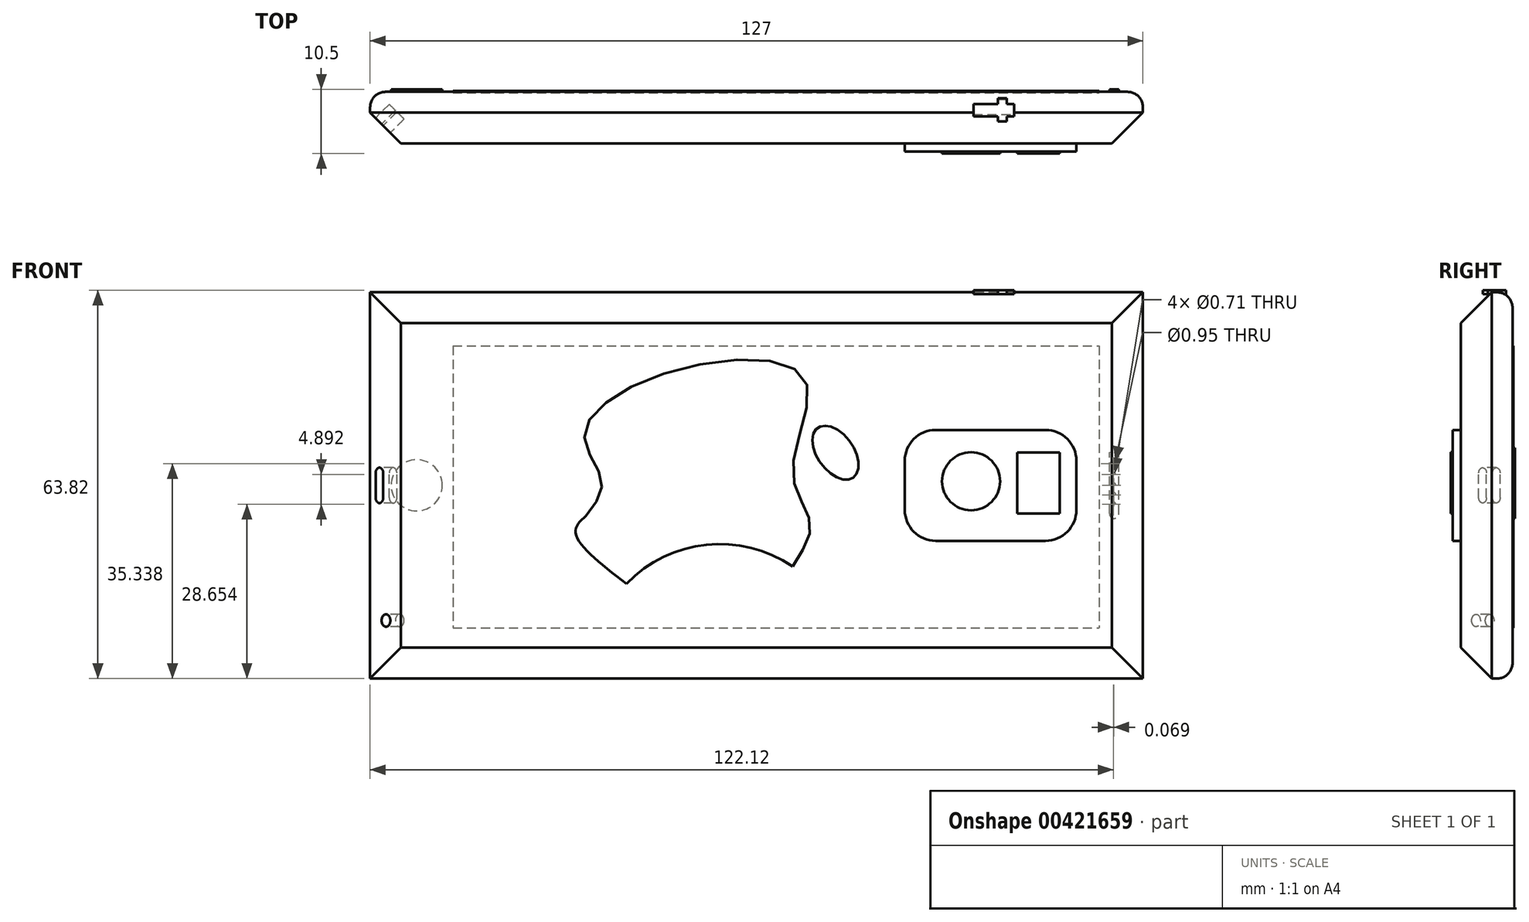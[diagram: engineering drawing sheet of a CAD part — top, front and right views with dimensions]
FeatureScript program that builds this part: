
annotation { "Feature Type Name" : "Feature", "Feature Type Description" : "" }
export const myFeature = defineFeature(function(context is Context, id is Id, definition is map)
    precondition{}
    {
        {
            var Q0;
            Q0=qCreatedBy(makeId("Front.planeOp"),FACE);
            var sketch = newSketch(context, id + "F0", { "sketchPlane" : qUnion([Q0])});
            skLineSegment(sketch, "E0.bottom", {"start": v(-64.83, 26.37) * mm, "end": v(62.17, 26.37) * mm});
            skLineSegment(sketch, "E0.top", {"start": v(-64.83, -37.13) * mm, "end": v(62.17, -37.13) * mm});
            skLineSegment(sketch, "E0.left", {"start": v(-64.83, 26.37) * mm, "end": v(-64.83, -37.13) * mm});
            skLineSegment(sketch, "E0.right", {"start": v(62.17, 26.37) * mm, "end": v(62.17, -37.13) * mm});
            skSolve(sketch);
        }
        {
            var Q0;
            Q0 = qSketchRegion(id + "F0", true);
            extrude(context, id + "F1", {"entities" : qUnion([Q0]), "depth" : 8.47 * mm});
        }
        {
            var Q0;
            Q0=makeQuery(id+"F1.opExtrude","CAP_FACE",FACE,{"disambiguationData":[OSD([sQuery(id+"F0.wireOp",EDGE,"E0.bottom"),sQuery(id+"F0.wireOp",EDGE,"E0.top"),sQuery(id+"F0.wireOp",EDGE,"E0.left"),sQuery(id+"F0.wireOp",EDGE,"E0.right")])],"isStart":true});
            fillet(context, id + "F2", {"entities" : qUnion([Q0]), "radius" : 2.54 * mm, "tangentPropagation" : true, "allowEdgeOverflow" : false});
        }
        {
            var Q0;
            Q0=makeQuery(id+"F1.opExtrude","CAP_FACE",FACE,{"disambiguationData":[OSD([sQuery(id+"F0.wireOp",EDGE,"E0.bottom"),sQuery(id+"F0.wireOp",EDGE,"E0.top"),sQuery(id+"F0.wireOp",EDGE,"E0.left"),sQuery(id+"F0.wireOp",EDGE,"E0.right")])],"isStart":true});
            var sketch = newSketch(context, id + "F3", { "sketchPlane" : qUnion([Q0])});
            skLineSegment(sketch, "E1.bottom", {"start": v(51.23, 17.56) * mm, "end": v(-54.97, 17.56) * mm});
            skLineSegment(sketch, "E1.top", {"start": v(51.23, -28.78) * mm, "end": v(-54.97, -28.78) * mm});
            skLineSegment(sketch, "E1.left", {"start": v(51.23, 17.56) * mm, "end": v(51.23, -28.78) * mm});
            skLineSegment(sketch, "E1.right", {"start": v(-54.97, 17.56) * mm, "end": v(-54.97, -28.78) * mm});
            skSolve(sketch);
        }
        {
            var Q0;
            Q0 = qSketchRegion(id + "F3", true);
            extrude(context, id + "F4", {"entities" : qUnion([Q0]), "endBound" : BoundingType.SYMMETRIC, "oppositeDirection" : true, "depth" : 0.28 * mm});
        }
        {
            var Q0;
            {var subQ0=sQuery(id+"F0.wireOp",EDGE,"E0.left");Q0=makeQuery(id+"F2.opFillet","BLEND_EDGE",EDGE,{"blendedFrom":[makeQuery(id+"F1.opExtrude","CAP_EDGE",EDGE,{"disambiguationData":[OSD([subQ0])],"isStart":true}),makeQuery(id+"F1.opExtrude","SWEPT_FACE",FACE,{"disambiguationData":[OSD([subQ0])]})],"blendedInto":[makeQuery(id+"F1.opExtrude","SWEPT_FACE",FACE,{"disambiguationData":[OSD([subQ0])]})]});}
            var Q1;
            Q1=makeQuery(id+"F1.opExtrude","CAP_EDGE",EDGE,{"disambiguationData":[OSD([sQuery(id+"F0.wireOp",EDGE,"E0.left")])],"isStart":false});
            var Q2;
            Q2=makeQuery(id+"F1.opExtrude","CAP_FACE",FACE,{"disambiguationData":[OSD([sQuery(id+"F0.wireOp",EDGE,"E0.bottom"),sQuery(id+"F0.wireOp",EDGE,"E0.top"),sQuery(id+"F0.wireOp",EDGE,"E0.left"),sQuery(id+"F0.wireOp",EDGE,"E0.right")])],"isStart":false});
            chamfer(context, id + "F5", {"entities" : qUnion([Q0, Q1, Q2]), "width" : 5.08 * mm, "tangentPropagation" : true});
        }
        {
            var Q0;
            Q0=makeQuery(id+"F1.opExtrude","CAP_FACE",FACE,{"disambiguationData":[OSD([sQuery(id+"F0.wireOp",EDGE,"E0.bottom"),sQuery(id+"F0.wireOp",EDGE,"E0.top"),sQuery(id+"F0.wireOp",EDGE,"E0.left"),sQuery(id+"F0.wireOp",EDGE,"E0.right")])],"isStart":true});
            var sketch = newSketch(context, id + "F6", { "sketchPlane" : qUnion([Q0])});
            skCircle(sketch, "E2", {"center": v(57.19, -5.38) * mm, "radius": 4.2 * mm});
            skPoint(sketch, "E2.centerSnap0", {"position": v(62.3, -5.38) * mm});
            skSolve(sketch);
        }
        {
            var Q0;
            Q0 = qSketchRegion(id + "F6", true);
            extrude(context, id + "F7", {"entities" : qUnion([Q0]), "depth" : 0.38 * mm});
        }
        {
            var Q0;
            Q0=makeQuery(id+"F1.opExtrude","CAP_FACE",FACE,{"disambiguationData":[OSD([sQuery(id+"F0.wireOp",EDGE,"E0.bottom"),sQuery(id+"F0.wireOp",EDGE,"E0.top"),sQuery(id+"F0.wireOp",EDGE,"E0.left"),sQuery(id+"F0.wireOp",EDGE,"E0.right")])],"isStart":true});
            var sketch = newSketch(context, id + "F8", { "sketchPlane" : qUnion([Q0])});
            skPoint(sketch, "E3.0.internal.snap0", {"position": v(-59.63, -5.38) * mm});
            skFitSpline(sketch, "E3", {"points": [v(-58.2, -5.38) * mm, v(-58.2, 0) * mm], "startDerivative": vector(0, 5.38) * mm, "endDerivative": vector(0, 5.38) * mm});
            skFitSpline(sketch, "E4", {"points": [v(-58.2, -5.38) * mm, v(-58.2, -10.03) * mm], "startDerivative": vector(0, -4.65) * mm, "endDerivative": vector(0, -4.65) * mm});
            skArc(sketch, "E5", {"start": v(-58.2, -10.03) * mm, "mid": v(-57.44, -10.81) * mm, "end": v(-56.67, -10.03) * mm});
            skLineSegment(sketch, "E6", {"start": v(-56.67, -10.03) * mm, "end": v(-56.67, 0) * mm});
            skArc(sketch, "E7", {"start": v(-56.67, 0) * mm, "mid": v(-57.44, 0.77) * mm, "end": v(-58.2, 0) * mm});
            skCircle(sketch, "E8", {"center": v(-57.33, -8.48) * mm, "radius": 0.36 * mm});
            skCircle(sketch, "E9", {"center": v(-57.36, -6.93) * mm, "radius": 0.36 * mm});
            skCircle(sketch, "E10", {"center": v(-57.36, -5.38) * mm, "radius": 0.36 * mm});
            skCircle(sketch, "E11", {"center": v(-57.3, -3.58) * mm, "radius": 0.36 * mm});
            skCircle(sketch, "E12", {"center": v(-57.3, -1.8) * mm, "radius": 0.48 * mm});
            skSolve(sketch);
        }
        {
            var Q0;
            Q0 = qSketchRegion(id + "F8", true);
            extrude(context, id + "F9", {"entities" : qUnion([Q0]), "depth" : 0.38 * mm});
        }
        {
            var Q0;
            Q0=makeQuery(id+"F1.opExtrude","CAP_FACE",FACE,{"disambiguationData":[OSD([sQuery(id+"F0.wireOp",EDGE,"E0.bottom"),sQuery(id+"F0.wireOp",EDGE,"E0.top"),sQuery(id+"F0.wireOp",EDGE,"E0.left"),sQuery(id+"F0.wireOp",EDGE,"E0.right")])],"isStart":false});
            var sketch = newSketch(context, id + "F10", { "sketchPlane" : qUnion([Q0])});
            skLineSegment(sketch, "E13.bottom", {"start": v(23.02, 3.74) * mm, "end": v(51.23, 3.74) * mm});
            skLineSegment(sketch, "E13.top", {"start": v(23.02, -14.5) * mm, "end": v(51.23, -14.5) * mm});
            skLineSegment(sketch, "E13.left", {"start": v(23.02, 3.74) * mm, "end": v(23.02, -14.5) * mm});
            skLineSegment(sketch, "E13.right", {"start": v(51.23, 3.74) * mm, "end": v(51.23, -14.5) * mm});
            skPoint(sketch, "E13.middle", {"position": v(37.13, -5.38) * mm});
            skPoint(sketch, "E13.middle.positionSnap0", {"position": v(57.09, -5.38) * mm});
            skPoint(sketch, "E13.centerSnap0", {"position": v(57.09, -5.38) * mm});
            skSolve(sketch);
        }
        {
            var Q0;
            Q0 = qSketchRegion(id + "F10", true);
            extrude(context, id + "F11", {"entities" : qUnion([Q0]), "depth" : 1.33 * mm});
        }
        {
            var Q0;
            Q0=makeQuery(id+"F11.opExtrude","SWEPT_EDGE",EDGE,{"disambiguationData":[OSD([sQuery(id+"F10.wireOp",EDGE,"E13.top"),sQuery(id+"F10.wireOp",EDGE,"E13.right")])]});
            var Q1;
            Q1=makeQuery(id+"F11.opExtrude","SWEPT_EDGE",EDGE,{"disambiguationData":[OSD([sQuery(id+"F10.wireOp",EDGE,"E13.bottom"),sQuery(id+"F10.wireOp",EDGE,"E13.right")])]});
            var Q2;
            Q2=makeQuery(id+"F11.opExtrude","SWEPT_EDGE",EDGE,{"disambiguationData":[OSD([sQuery(id+"F10.wireOp",EDGE,"E13.top"),sQuery(id+"F10.wireOp",EDGE,"E13.left")])]});
            var Q3;
            Q3=makeQuery(id+"F11.opExtrude","SWEPT_EDGE",EDGE,{"disambiguationData":[OSD([sQuery(id+"F10.wireOp",EDGE,"E13.bottom"),sQuery(id+"F10.wireOp",EDGE,"E13.left")])]});
            fillet(context, id + "F12", {"entities" : qUnion([Q0, Q1, Q2, Q3]), "radius" : 5.08 * mm, "tangentPropagation" : true, "allowEdgeOverflow" : false});
        }
        {
            var Q0;
            Q0=makeQuery(id+"F11.opExtrude","CAP_FACE",FACE,{"disambiguationData":[OSD([sQuery(id+"F10.wireOp",EDGE,"E13.bottom"),sQuery(id+"F10.wireOp",EDGE,"E13.top"),sQuery(id+"F10.wireOp",EDGE,"E13.left"),sQuery(id+"F10.wireOp",EDGE,"E13.right")])],"isStart":false});
            var sketch = newSketch(context, id + "F13", { "sketchPlane" : qUnion([Q0])});
            skLineSegment(sketch, "E14.bottom", {"start": v(41.49, 0) * mm, "end": v(48.48, 0) * mm});
            skLineSegment(sketch, "E14.top", {"start": v(41.49, -10) * mm, "end": v(48.48, -10) * mm});
            skLineSegment(sketch, "E14.left", {"start": v(41.49, 0) * mm, "end": v(41.49, -10) * mm});
            skLineSegment(sketch, "E14.right", {"start": v(48.48, 0) * mm, "end": v(48.48, -10) * mm});
            skPoint(sketch, "E14.middle", {"position": v(44.98, -5) * mm});
            skCircle(sketch, "E15", {"center": v(33.92, -4.7) * mm, "radius": 4.77 * mm});
            skSolve(sketch);
        }
        {
            var Q0;
            Q0 = qSketchRegion(id + "F13", true);
            extrude(context, id + "F14", {"entities" : qUnion([Q0]), "depth" : 0.32 * mm});
        }
        {
            var Q0;
            Q0=makeQuery(id+"F5.opChamfer","BLEND_FACE",FACE,{"disambiguationData":[OSD([sQuery(id+"F0.wireOp",EDGE,"E0.left")])]});
            var sketch = newSketch(context, id + "F15", { "sketchPlane" : qUnion([Q0])});
            skLineSegment(sketch, "E16.bottom", {"start": v(-40.39, -7.39) * mm, "end": v(-42.18, -7.39) * mm});
            skLineSegment(sketch, "E16.top", {"start": v(-40.39, -3.37) * mm, "end": v(-42.18, -3.37) * mm});
            skLineSegment(sketch, "E16.left", {"start": v(-40.39, -7.39) * mm, "end": v(-40.39, -3.37) * mm});
            skLineSegment(sketch, "E16.right", {"start": v(-42.18, -7.39) * mm, "end": v(-42.18, -3.37) * mm});
            skPoint(sketch, "E16.middle", {"position": v(-41.28, -5.38) * mm});
            skPoint(sketch, "E16.middle.positionSnap0", {"position": v(-43.45, -5.38) * mm});
            skPoint(sketch, "E16.centerSnap0", {"position": v(-43.45, -5.38) * mm});
            skArc(sketch, "E17", {"start": v(-42.18, -7.39) * mm, "mid": v(-41.28, -8.28) * mm, "end": v(-40.39, -7.39) * mm});
            skArc(sketch, "E18", {"start": v(-40.39, -3.37) * mm, "mid": v(-41.28, -2.47) * mm, "end": v(-42.18, -3.37) * mm});
            skSolve(sketch);
        }
        {
            var Q0;
            Q0 = qSketchRegion(id + "F15", true);
            extrude(context, id + "F16", {"entities" : qUnion([Q0]), "operationType" : NewBodyOperationType.REMOVE, "oppositeDirection" : true, "depth" : 3.17 * mm});
        }
        {
            var Q0;
            Q0=makeQuery(id+"F5.opChamfer","BLEND_FACE",FACE,{"disambiguationData":[OSD([sQuery(id+"F0.wireOp",EDGE,"E0.left")])]});
            var sketch = newSketch(context, id + "F17", { "sketchPlane" : qUnion([Q0])});
            skCircle(sketch, "E19", {"center": v(-39.75, -27.59) * mm, "radius": 1.02 * mm});
            skSolve(sketch);
        }
        {
            var Q0;
            Q0 = qSketchRegion(id + "F17", true);
            extrude(context, id + "F18", {"entities" : qUnion([Q0]), "operationType" : NewBodyOperationType.REMOVE, "oppositeDirection" : true, "depth" : 3.17 * mm});
        }
        {
            var Q0;
            Q0=makeQuery(id+"F1.opExtrude","SWEPT_FACE",FACE,{"disambiguationData":[OSD([sQuery(id+"F0.wireOp",EDGE,"E0.bottom")])]});
            var sketch = newSketch(context, id + "F19", { "sketchPlane" : qUnion([Q0])});
            skLineSegment(sketch, "E20.bottom", {"start": v(41, -2) * mm, "end": v(34.3, -2) * mm});
            skLineSegment(sketch, "E20.top", {"start": v(41, -4.06) * mm, "end": v(34.3, -4.06) * mm});
            skLineSegment(sketch, "E20.left", {"start": v(41, -2) * mm, "end": v(41, -4.06) * mm});
            skLineSegment(sketch, "E20.right", {"start": v(34.3, -2) * mm, "end": v(34.3, -4.06) * mm});
            skLineSegment(sketch, "E21.bottom", {"start": v(39.76, -1.08) * mm, "end": v(38.32, -1.08) * mm});
            skLineSegment(sketch, "E21.top", {"start": v(39.76, -4.89) * mm, "end": v(38.32, -4.89) * mm});
            skLineSegment(sketch, "E21.left", {"start": v(39.76, -1.08) * mm, "end": v(39.76, -4.89) * mm});
            skLineSegment(sketch, "E21.right", {"start": v(38.32, -1.08) * mm, "end": v(38.32, -4.89) * mm});
            skSolve(sketch);
        }
        {
            var Q0;
            Q0 = qSketchRegion(id + "F19", true);
            extrude(context, id + "F20", {"entities" : qUnion([Q0]), "operationType" : NewBodyOperationType.ADD, "endBound" : BoundingType.SYMMETRIC, "depth" : 0.64 * mm});
        }
        {
            var Q0;
            Q0=makeQuery(id+"F1.opExtrude","CAP_FACE",FACE,{"disambiguationData":[OSD([sQuery(id+"F0.wireOp",EDGE,"E0.bottom"),sQuery(id+"F0.wireOp",EDGE,"E0.top"),sQuery(id+"F0.wireOp",EDGE,"E0.left"),sQuery(id+"F0.wireOp",EDGE,"E0.right")])],"isStart":false});
            var sketch = newSketch(context, id + "F21", { "sketchPlane" : qUnion([Q0])});
            skFitSpline(sketch, "E22", {"points": [v(-29.36, -10.36) * mm, v(-26.77, -4.6) * mm, v(-29.64, 2.88) * mm, v(-15.83, 13.24) * mm, v(6.62, 12.09) * mm, v(4.6, -3.17) * mm, v(7.48, -11.51) * mm, v(4.6, -18.7) * mm], "startDerivative": vector(41.52, 53.03) * mm, "endDerivative": vector(-40.99, -62.99) * mm});
            skFitSpline(sketch, "E23", {"points": [v(-29.36, -10.36) * mm, v(-31.08, -13.18) * mm, v(-22.7, -21.56) * mm], "startDerivative": vector(-8.07, -7.35) * mm, "endDerivative": vector(18.62, -14.32) * mm});
            skArc(sketch, "E24", {"start": v(4.6, -18.7) * mm, "mid": v(-9.57, -15.13) * mm, "end": v(-22.7, -21.56) * mm});
            skEllipse(sketch, "E25", {"center": v(11.65, 0) * mm, "majorRadius": 5.02 * mm, "minorRadius": 3 * mm, "majorAxis": v(0.58, -0.81)});
            skSolve(sketch);
        }
        {
            var Q0;
            Q0 = qSketchRegion(id + "F21", true);
            extrude(context, id + "F22", {"entities" : qUnion([Q0]), "depth" : 0.03 * mm});
        }
    });
